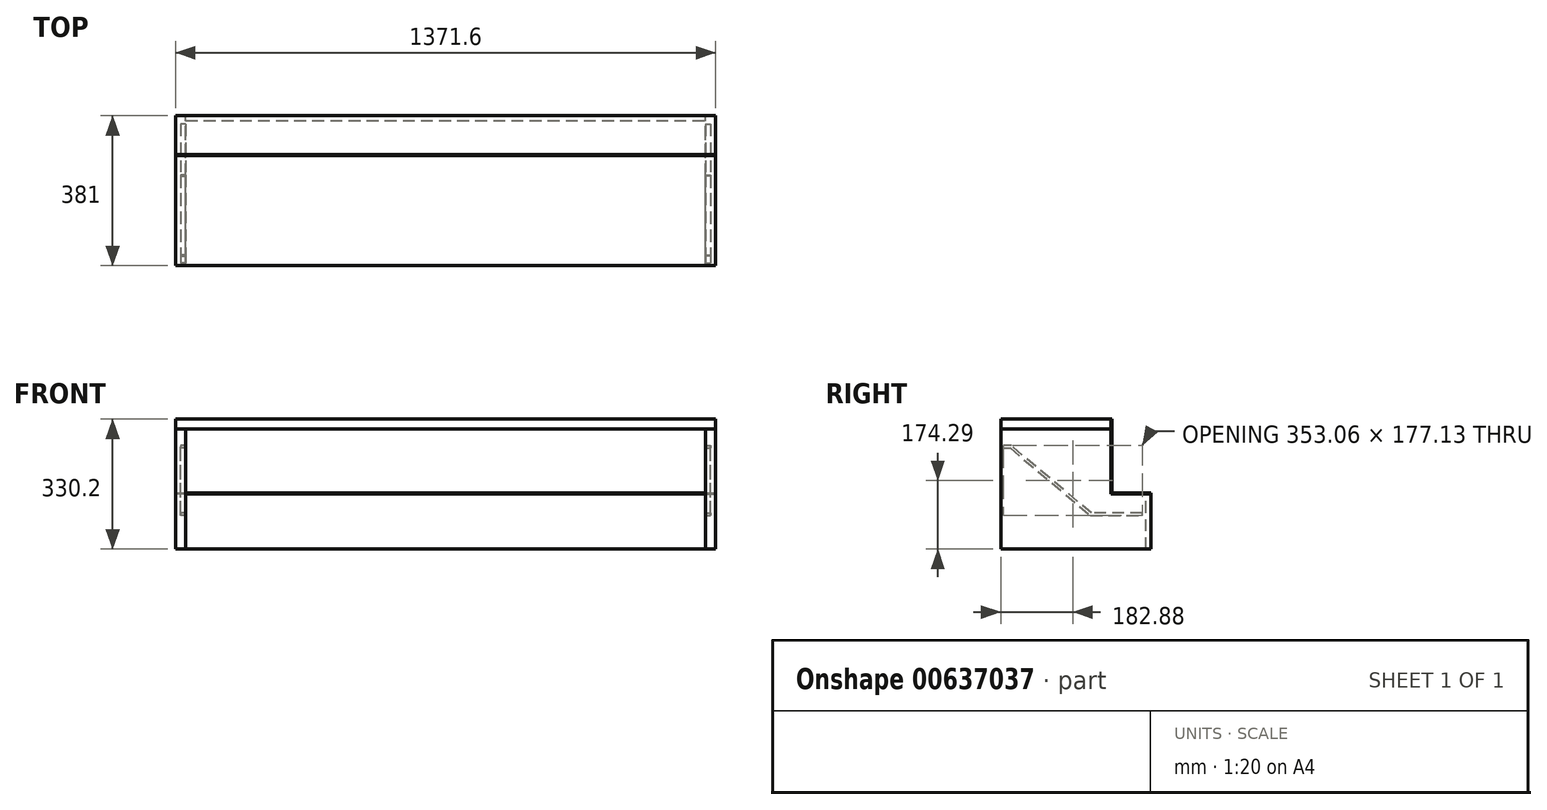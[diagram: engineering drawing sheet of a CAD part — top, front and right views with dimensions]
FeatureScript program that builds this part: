
annotation { "Feature Type Name" : "Feature", "Feature Type Description" : "" }
export const myFeature = defineFeature(function(context is Context, id is Id, definition is map)
    precondition{}
    {
        {
            var Q0;
            Q0=qCreatedBy(makeId("Right.planeOp"),FACE);
            cPlane(context, id + "F0", {"entities" : qUnion([Q0]), "cplaneType" : CPlaneType.OFFSET, "offset" : 685.8 * mm, "width" : 152.4 * mm, "height" : 152.4 * mm});
        }
        {
            var Q0;
            Q0=qCreatedBy(id+"F0.planeOp",FACE);
            var sketch = newSketch(context, id + "F1", { "sketchPlane" : qUnion([Q0])});
            skLineSegment(sketch, "E0.top", {"start": v(0, 0) * mm, "end": v(381, 0) * mm});
            skLineSegment(sketch, "E0.left", {"start": v(0, 304.8) * mm, "end": v(0, 0) * mm});
            skLineSegment(sketch, "E1", {"start": v(279.4, 304.8) * mm, "end": v(279.4, 139.7) * mm});
            skLineSegment(sketch, "E2", {"start": v(279.4, 139.7) * mm, "end": v(381, 139.7) * mm});
            skLineSegment(sketch, "E3", {"start": v(0, 304.8) * mm, "end": v(279.4, 304.8) * mm});
            skLineSegment(sketch, "E4", {"start": v(381, 139.7) * mm, "end": v(381, 0) * mm});
            skSolve(sketch);
        }
        {
            var Q0;
            Q0 = qSketchRegion(id + "F1", true);
            extrude(context, id + "F2", {"entities" : qUnion([Q0]), "oppositeDirection" : true, "depth" : 25.4 * mm, "offsetDistance" : 25.4 * mm});
        }
        {
            var Q0;
            Q0=makeQuery(id+"F2.opExtrude","CAP_FACE",FACE,{"disambiguationData":[OSD([sQuery(id+"F1.wireOp",EDGE,"E0.top"),sQuery(id+"F1.wireOp",EDGE,"E0.left"),sQuery(id+"F1.wireOp",EDGE,"E1"),sQuery(id+"F1.wireOp",EDGE,"E2"),sQuery(id+"F1.wireOp",EDGE,"E3"),sQuery(id+"F1.wireOp",EDGE,"E4")])],"isStart":false});
            cPlane(context, id + "F3", {"entities" : qUnion([Q0]), "cplaneType" : CPlaneType.OFFSET, "offset" : 0 * mm, "width" : 152.4 * mm, "height" : 152.4 * mm});
        }
        {
            var Q0;
            Q0=qCreatedBy(id+"F3.planeOp",FACE);
            var sketch = newSketch(context, id + "F4", { "sketchPlane" : qUnion([Q0])});
            skLineSegment(sketch, "E5", {"start": v(-25.4, 259.68) * mm, "end": v(-228.93, 88.9) * mm});
            skLineSegment(sketch, "E6", {"start": v(-92.7, 356.22) * mm, "end": v(-92.7, 203.2) * mm});
            skLineSegment(sketch, "E7", {"start": v(-92.7, 203.2) * mm, "end": v(0, 203.2) * mm});
            skLineSegment(sketch, "E8", {"start": v(-228.93, 88.9) * mm, "end": v(-359.41, 88.9) * mm});
            skLineSegment(sketch, "E9", {"start": v(-25.4, 259.68) * mm, "end": v(-6.35, 259.68) * mm});
            skSolve(sketch);
        }
        {
            var Q0;
            Q0=sQuery(id+"F4.wireOp",EDGE,"E8");
            var Q1;
            Q1=sQuery(id+"F4.wireOp",VERTEX,"E8.end");
            cPlane(context, id + "F5", {"entities" : qUnion([Q0, Q1]), "cplaneType" : CPlaneType.LINE_POINT, "offset" : 25.4 * mm, "width" : 152.4 * mm, "height" : 152.4 * mm});
        }
        {
            var Q0;
            Q0=qCreatedBy(id+"F5.planeOp",FACE);
            var sketch = newSketch(context, id + "F6", { "sketchPlane" : qUnion([Q0])});
            skLineSegment(sketch, "E10.bottom", {"start": v(-647.7, 92.07) * mm, "end": v(-673.1, 92.07) * mm});
            skLineSegment(sketch, "E10.top", {"start": v(-647.7, 85.72) * mm, "end": v(-673.1, 85.72) * mm});
            skLineSegment(sketch, "E10.left", {"start": v(-647.7, 92.07) * mm, "end": v(-647.7, 85.72) * mm});
            skLineSegment(sketch, "E10.right", {"start": v(-673.1, 92.07) * mm, "end": v(-673.1, 85.72) * mm});
            skPoint(sketch, "E10.middle", {"position": v(-660.4, 88.9) * mm});
            skSolve(sketch);
        }
        {
            var Q0;
            Q0=makeQuery(id+"F6.imprint","IMPRINT",FACE,{"disambiguationData":[TD([[makeQuery(id+"F6.imprint","IMPRINT",EDGE,{"derivedFrom":sQuery(id+"F6.wireOp",EDGE,"E10.bottom")}),1.0]])]});
            var Q1;
            Q1=sQuery(id+"F4.wireOp",EDGE,"E8");
            var Q2;
            Q2=sQuery(id+"F4.wireOp",EDGE,"E5");
            var Q3;
            Q3=sQuery(id+"F4.wireOp",EDGE,"E9");
            sweep(context, id + "F7", {"operationType" : NewBodyOperationType.REMOVE, "profiles" : qUnion([Q0]), "path" : qUnion([Q1, Q2, Q3])});
        }
        {
            var Q0;
            Q0=makeQuery(id+"F2.opExtrude","SWEPT_BODY",BODY,{"disambiguationData":[OSD([sQuery(id+"F1.wireOp",EDGE,"E0.top"),sQuery(id+"F1.wireOp",EDGE,"E0.left"),sQuery(id+"F1.wireOp",EDGE,"E1"),sQuery(id+"F1.wireOp",EDGE,"E2"),sQuery(id+"F1.wireOp",EDGE,"E3"),sQuery(id+"F1.wireOp",EDGE,"E4")])]});
            var Q1;
            Q1=qCreatedBy(makeId("Right.planeOp"),FACE);
            mirror(context, id + "F8", {"operationType" : NewBodyOperationType.ADD, "entities" : qUnion([Q0]), "mirrorPlane" : qUnion([Q1])});
        }
        {
            var Q0;
            Q0=makeQuery(id+"F8.opPattern","COPY",FACE,{"derivedFrom":makeQuery(id+"F2.opExtrude","SWEPT_FACE",FACE,{"disambiguationData":[OSD([sQuery(id+"F1.wireOp",EDGE,"E3")])]}),"instanceName":"1"});
            cPlane(context, id + "F9", {"entities" : qUnion([Q0]), "cplaneType" : CPlaneType.OFFSET, "offset" : 25.4 * mm, "width" : 152.4 * mm, "height" : 152.4 * mm});
        }
        {
            var Q0;
            Q0=qCreatedBy(id+"F9.planeOp",FACE);
            var sketch = newSketch(context, id + "F10", { "sketchPlane" : qUnion([Q0])});
            skLineSegment(sketch, "E11.bottom", {"start": v(685.8, 0) * mm, "end": v(-685.8, 0) * mm});
            skLineSegment(sketch, "E11.top", {"start": v(685.8, 279.4) * mm, "end": v(-685.8, 279.4) * mm});
            skLineSegment(sketch, "E11.left", {"start": v(685.8, 0) * mm, "end": v(685.8, 279.4) * mm});
            skLineSegment(sketch, "E11.right", {"start": v(-685.8, 0) * mm, "end": v(-685.8, 279.4) * mm});
            skPoint(sketch, "E11.middle", {"position": v(0, 139.7) * mm});
            skSolve(sketch);
        }
        {
            var Q0;
            Q0 = qSketchRegion(id + "F10", true);
            extrude(context, id + "F11", {"entities" : qUnion([Q0]), "oppositeDirection" : true, "depth" : 25.4 * mm, "offsetDistance" : 25.4 * mm});
        }
        {
            var Q0;
            Q0=makeQuery(id+"F8.opPattern","COPY",FACE,{"derivedFrom":makeQuery(id+"F2.opExtrude","SWEPT_FACE",FACE,{"disambiguationData":[OSD([sQuery(id+"F1.wireOp",EDGE,"E2")])]}),"instanceName":"1"});
            cPlane(context, id + "F12", {"entities" : qUnion([Q0]), "cplaneType" : CPlaneType.OFFSET, "offset" : 3.17 * mm, "width" : 152.4 * mm, "height" : 152.4 * mm});
        }
        {
            var Q0;
            Q0=qCreatedBy(id+"F12.planeOp",FACE);
            var sketch = newSketch(context, id + "F13", { "sketchPlane" : qUnion([Q0])});
            skLineSegment(sketch, "E12.bottom", {"start": v(685.8, 279.4) * mm, "end": v(-685.8, 279.4) * mm});
            skLineSegment(sketch, "E12.top", {"start": v(685.8, 381) * mm, "end": v(-685.8, 381) * mm});
            skLineSegment(sketch, "E12.left", {"start": v(685.8, 279.4) * mm, "end": v(685.8, 381) * mm});
            skLineSegment(sketch, "E12.right", {"start": v(-685.8, 279.4) * mm, "end": v(-685.8, 381) * mm});
            skPoint(sketch, "E12.middle", {"position": v(0, 330.2) * mm});
            skSolve(sketch);
        }
        {
            var Q0;
            Q0 = qSketchRegion(id + "F13", true);
            var Q1;
            Q1=makeQuery(id+"F8.opPattern","COPY",FACE,{"derivedFrom":makeQuery(id+"F2.opExtrude","SWEPT_FACE",FACE,{"disambiguationData":[OSD([sQuery(id+"F1.wireOp",EDGE,"E2")])]}),"instanceName":"1"});
            var Q2;
            Q2=makeQuery(id+"F8.opPattern","COPY",BODY,{"derivedFrom":makeQuery(id+"F2.opExtrude","SWEPT_BODY",BODY,{"disambiguationData":[OSD([sQuery(id+"F1.wireOp",EDGE,"E0.top"),sQuery(id+"F1.wireOp",EDGE,"E0.left"),sQuery(id+"F1.wireOp",EDGE,"E1"),sQuery(id+"F1.wireOp",EDGE,"E2"),sQuery(id+"F1.wireOp",EDGE,"E3"),sQuery(id+"F1.wireOp",EDGE,"E4")])]}),"instanceName":"1"});
            extrude(context, id + "F14", {"entities" : qUnion([Q0]), "endBound" : BoundingType.UP_TO_SURFACE, "oppositeDirection" : true, "depth" : 25.4 * mm, "endBoundEntityFace" : qUnion([Q1]), "endBoundEntityBody" : qUnion([Q2]), "offsetDistance" : 25.4 * mm});
        }
        {
            var Q0;
            Q0=makeQuery(id+"F2.opExtrude","SWEPT_FACE",FACE,{"disambiguationData":[OSD([sQuery(id+"F1.wireOp",EDGE,"E1")])]});
            cPlane(context, id + "F15", {"entities" : qUnion([Q0]), "cplaneType" : CPlaneType.OFFSET, "offset" : 3.17 * mm, "width" : 152.4 * mm, "height" : 152.4 * mm});
        }
        {
            var Q0;
            Q0=qCreatedBy(id+"F15.planeOp",FACE);
            var sketch = newSketch(context, id + "F16", { "sketchPlane" : qUnion([Q0])});
            skLineSegment(sketch, "E13.bottom", {"start": v(685.8, 142.88) * mm, "end": v(-685.8, 142.88) * mm});
            skLineSegment(sketch, "E13.top", {"start": v(685.8, 330.2) * mm, "end": v(-685.8, 330.2) * mm});
            skLineSegment(sketch, "E13.left", {"start": v(685.8, 142.88) * mm, "end": v(685.8, 330.2) * mm});
            skLineSegment(sketch, "E13.right", {"start": v(-685.8, 142.88) * mm, "end": v(-685.8, 330.2) * mm});
            skPoint(sketch, "E13.middle", {"position": v(0, 236.54) * mm});
            skSolve(sketch);
        }
        {
            var Q0;
            Q0 = qSketchRegion(id + "F16", true);
            var Q1;
            Q1=makeQuery(id+"F2.opExtrude","SWEPT_FACE",FACE,{"disambiguationData":[OSD([sQuery(id+"F1.wireOp",EDGE,"E1")])]});
            extrude(context, id + "F17", {"entities" : qUnion([Q0]), "endBound" : BoundingType.UP_TO_SURFACE, "oppositeDirection" : true, "depth" : 25.4 * mm, "endBoundEntityFace" : qUnion([Q1]), "offsetDistance" : 25.4 * mm});
        }
        {
            var Q0;
            Q0=makeQuery(id+"F2.opExtrude","SWEPT_FACE",FACE,{"disambiguationData":[OSD([sQuery(id+"F1.wireOp",EDGE,"E4")])]});
            cPlane(context, id + "F18", {"entities" : qUnion([Q0]), "cplaneType" : CPlaneType.OFFSET, "offset" : 0 * mm, "width" : 152.4 * mm, "height" : 152.4 * mm});
        }
        {
            var Q0;
            Q0=qCreatedBy(id+"F18.planeOp",FACE);
            var sketch = newSketch(context, id + "F19", { "sketchPlane" : qUnion([Q0])});
            skLineSegment(sketch, "E14.bottom", {"start": v(660.4, 0) * mm, "end": v(-660.4, 0) * mm});
            skLineSegment(sketch, "E14.top", {"start": v(660.4, 139.7) * mm, "end": v(-660.4, 139.7) * mm});
            skLineSegment(sketch, "E14.left", {"start": v(660.4, 0) * mm, "end": v(660.4, 139.7) * mm});
            skLineSegment(sketch, "E14.right", {"start": v(-660.4, 0) * mm, "end": v(-660.4, 139.7) * mm});
            skPoint(sketch, "E14.middle", {"position": v(0, 69.85) * mm});
            skSolve(sketch);
        }
        {
            var Q0;
            Q0 = qSketchRegion(id + "F19", true);
            extrude(context, id + "F20", {"entities" : qUnion([Q0]), "oppositeDirection" : true, "depth" : 12.7 * mm, "offsetDistance" : 25.4 * mm});
        }
    });
